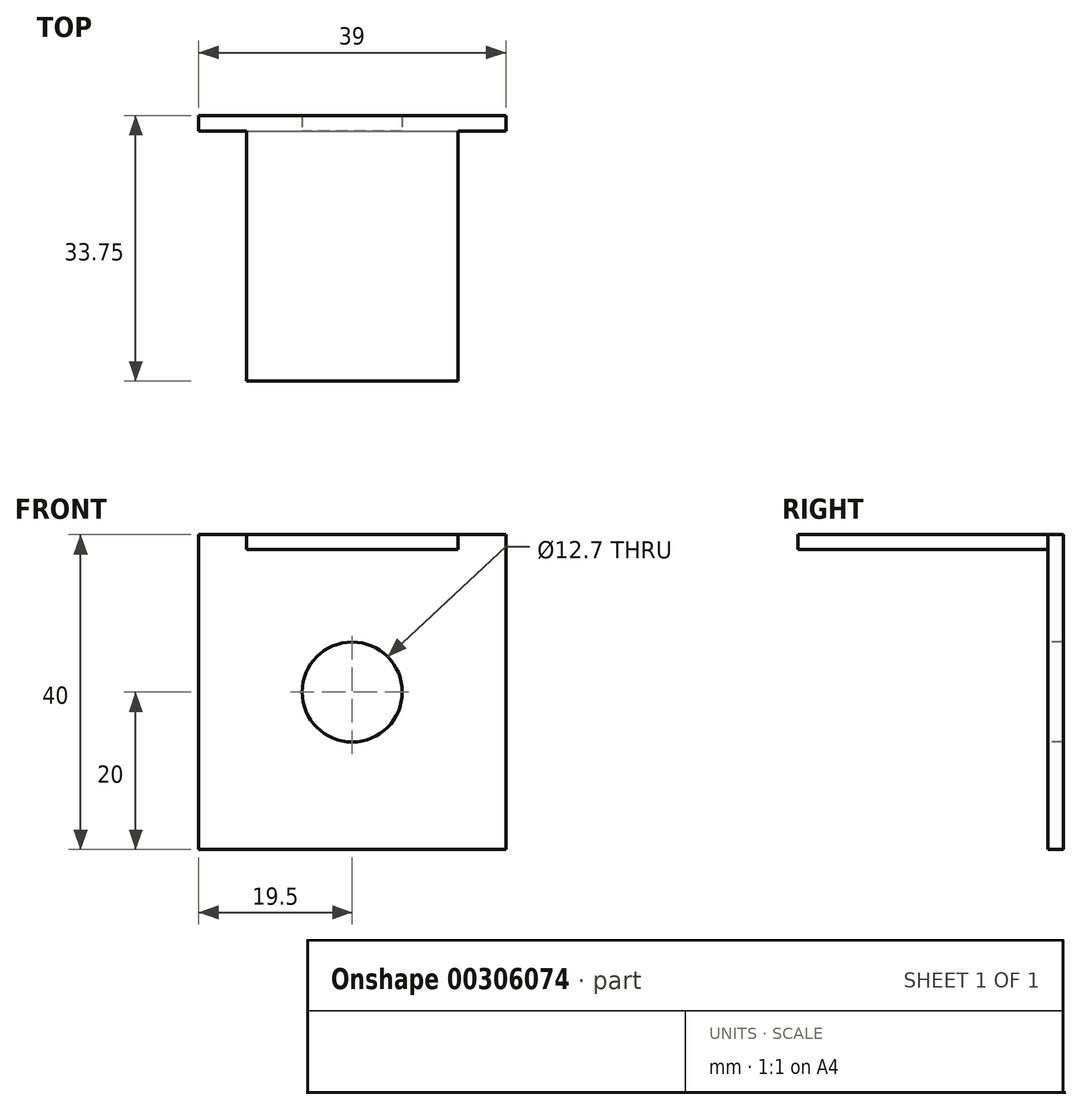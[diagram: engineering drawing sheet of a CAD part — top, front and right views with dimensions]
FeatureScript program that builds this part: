
annotation { "Feature Type Name" : "Feature", "Feature Type Description" : "" }
export const myFeature = defineFeature(function(context is Context, id is Id, definition is map)
    precondition{}
    {
        {
            var Q0;
            Q0=qCreatedBy(makeId("Front.planeOp"),FACE);
            var sketch = newSketch(context, id + "F0", { "sketchPlane" : qUnion([Q0])});
            skLineSegment(sketch, "E0.bottom", {"start": v(-15.02, 4.03) * mm, "end": v(23.98, 4.03) * mm});
            skLineSegment(sketch, "E0.top", {"start": v(-15.02, -35.97) * mm, "end": v(23.98, -35.97) * mm});
            skLineSegment(sketch, "E0.left", {"start": v(-15.02, 4.03) * mm, "end": v(-15.02, -35.97) * mm});
            skLineSegment(sketch, "E0.right", {"start": v(23.98, 4.03) * mm, "end": v(23.98, -35.97) * mm});
            skSolve(sketch);
        }
        {
            var Q0;
            Q0 = qSketchRegion(id + "F0", true);
            extrude(context, id + "F1", {"entities" : qUnion([Q0]), "depth" : 2 * mm});
        }
        {
            var Q0;
            Q0=makeQuery(id+"F1.opExtrude","CAP_FACE",FACE,{"disambiguationData":[OSD([sQuery(id+"F0.wireOp",EDGE,"E0.bottom"),sQuery(id+"F0.wireOp",EDGE,"E0.top"),sQuery(id+"F0.wireOp",EDGE,"E0.left"),sQuery(id+"F0.wireOp",EDGE,"E0.right")])],"isStart":false});
            var sketch = newSketch(context, id + "F2", { "sketchPlane" : qUnion([Q0])});
            skLineSegment(sketch, "E1", {"start": v(-8.93, 2.11) * mm, "end": v(17.89, 2.11) * mm});
            skLineSegment(sketch, "E2", {"start": v(-8.93, 2.11) * mm, "end": v(-8.93, 4.03) * mm});
            skLineSegment(sketch, "E3", {"start": v(-8.93, 4.03) * mm, "end": v(17.89, 4.03) * mm});
            skLineSegment(sketch, "E4", {"start": v(17.89, 2.11) * mm, "end": v(17.89, 4.03) * mm});
            skSolve(sketch);
        }
        {
            var Q0;
            Q0 = qSketchRegion(id + "F2", true);
            extrude(context, id + "F3", {"entities" : qUnion([Q0]), "operationType" : NewBodyOperationType.ADD, "depth" : 31.75 * mm});
        }
        {
            var Q0;
            Q0=makeQuery(id+"F1.opExtrude","CAP_FACE",FACE,{"disambiguationData":[OSD([sQuery(id+"F0.wireOp",EDGE,"E0.bottom"),sQuery(id+"F0.wireOp",EDGE,"E0.top"),sQuery(id+"F0.wireOp",EDGE,"E0.left"),sQuery(id+"F0.wireOp",EDGE,"E0.right")])],"isStart":false});
            var sketch = newSketch(context, id + "F4", { "sketchPlane" : qUnion([Q0])});
            skLineSegment(sketch, "E5", {"start": v(4.48, 2.11) * mm, "end": v(4.48, -6.52) * mm});
            skCircle(sketch, "E6", {"center": v(4.48, -15.97) * mm, "radius": 6.35 * mm});
            skPoint(sketch, "E6.centerSnap0", {"position": v(-15.02, -15.97) * mm});
            skCircle(sketch, "E7", {"center": v(4.48, -6.52) * mm, "radius": 1.9 * mm});
            skCircle(sketch, "E8", {"center": v(4.48, -27.33) * mm, "radius": 1.9 * mm});
            skCircle(sketch, "E9.1.0", {"center": v(-4.97, -15.97) * mm, "radius": 1.9 * mm});
            skCircle(sketch, "E9.1.1", {"center": v(15.84, -15.97) * mm, "radius": 1.9 * mm});
            skSolve(sketch);
        }
        {
            var Q0;
            Q0=sQuery(id+"F4.wireOp",VERTEX,"E6.center");
            var Q1;
            Q1=makeQuery(id+"F1.opExtrude","SWEPT_BODY",BODY,{"disambiguationData":[OSD([sQuery(id+"F0.wireOp",EDGE,"E0.bottom"),sQuery(id+"F0.wireOp",EDGE,"E0.top"),sQuery(id+"F0.wireOp",EDGE,"E0.left"),sQuery(id+"F0.wireOp",EDGE,"E0.right")])]});
            hole(context, id + "F5", {"style" : HoleStyle.SIMPLE, "endStyle" : HoleEndStyle.BLIND, "holeDiameter" : 12.7 * mm, "holeDepth" : 76.2 * mm, "tappedDepth" : 12.7 * mm, "tapClearance" : 3, "startFromSketch" : true, "locations" : qUnion([Q0]), "scope" : qUnion([Q1])});
        }
    });
